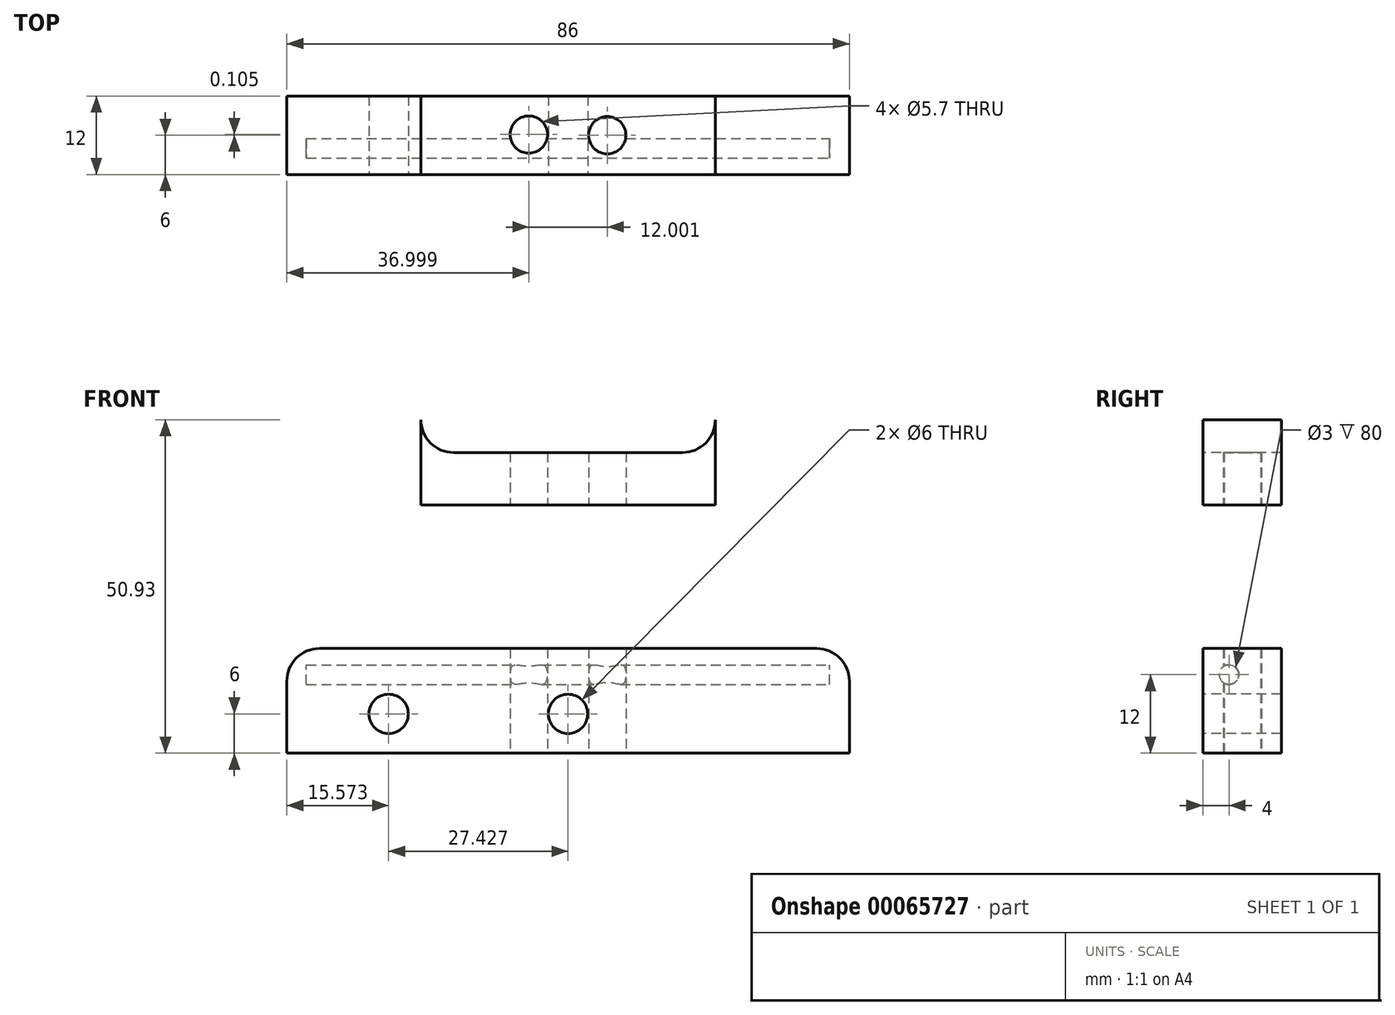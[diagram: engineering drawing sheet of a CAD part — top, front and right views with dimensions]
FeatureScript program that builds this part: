
annotation { "Feature Type Name" : "Feature", "Feature Type Description" : "" }
export const myFeature = defineFeature(function(context is Context, id is Id, definition is map)
    precondition{}
    {
        {
            var Q0;
            Q0=qCreatedBy(makeId("Top.planeOp"),FACE);
            var sketch = newSketch(context, id + "F0", { "sketchPlane" : qUnion([Q0])});
            skPoint(sketch, "E0.rect.middle", {"position": v(0, 0) * mm});
            skLineSegment(sketch, "E1", {"start": v(0, 0) * mm, "end": v(0, 2) * mm});
            skLineSegment(sketch, "E2", {"start": v(0, 2) * mm, "end": v(12, 2) * mm, "construction": true});
            skPoint(sketch, "E3.rect.middle", {"position": v(0, 2) * mm});
            skLineSegment(sketch, "E4", {"start": v(35, -4) * mm, "end": v(20.22, -4) * mm});
            skLineSegment(sketch, "E5", {"start": v(35, 8) * mm, "end": v(-35, 8) * mm});
            skPoint(sketch, "E6.rect.middle", {"position": v(0, 8) * mm});
            skLineSegment(sketch, "E7", {"start": v(-35, 8) * mm, "end": v(35, 8) * mm});
            skLineSegment(sketch, "E8.MirrorCS", {"start": v(19.85, 8) * mm, "end": v(20.22, 8) * mm});
            skLineSegment(sketch, "E9.trimOffspring", {"start": v(-20.22, -4) * mm, "end": v(-35, -4) * mm});
            skLineSegment(sketch, "E10.trimOffspring", {"start": v(19.85, -4) * mm, "end": v(-19.85, -4) * mm});
            skLineSegment(sketch, "E11", {"start": v(-19.85, -4) * mm, "end": v(-20.22, -4) * mm});
            skLineSegment(sketch, "E12", {"start": v(19.85, -4) * mm, "end": v(20.22, -4) * mm});
            skPoint(sketch, "E13.left.start.orphan", {"position": v(-19.85, 8) * mm});
            skPoint(sketch, "E14.start.orphan", {"position": v(-20.22, 8) * mm});
            skLineSegment(sketch, "E15.bottom", {"start": v(-35, 8) * mm, "end": v(-43, 8) * mm});
            skLineSegment(sketch, "E15.top", {"start": v(-35, -4) * mm, "end": v(-43, -4) * mm});
            skLineSegment(sketch, "E15.right", {"start": v(-43, 8) * mm, "end": v(-43, -4) * mm});
            skLineSegment(sketch, "E16.bottom", {"start": v(35, 8) * mm, "end": v(43, 8) * mm});
            skLineSegment(sketch, "E16.top", {"start": v(35, -4) * mm, "end": v(43, -4) * mm});
            skLineSegment(sketch, "E16.right", {"start": v(43, 8) * mm, "end": v(43, -4) * mm});
            skCircle(sketch, "E17", {"center": v(6, 2) * mm, "radius": 2.85 * mm});
            skCircle(sketch, "E18", {"center": v(-6, 2.1) * mm, "radius": 2.85 * mm});
            skSolve(sketch);
        }
        {
            var Q0;
            {var subQ4=sQuery(id+"F0.wireOp",EDGE,"E6.rect.right");Q0=makeQuery(id+"F0.imprint","IMPRINT",FACE,{"disambiguationData":[TD([[makeQuery(id+"F0.imprint","IMPRINT",EDGE,{"derivedFrom":subQ4}),1.0]])]});}
            var Q1;
            {var subQ3=sQuery(id+"F0.wireOp",EDGE,"E13.right");Q1=makeQuery(id+"F0.imprint","IMPRINT",FACE,{"disambiguationData":[TD([[makeQuery(id+"F0.imprint","IMPRINT",EDGE,{"derivedFrom":subQ3}),-1.0]])]});}
            var Q2;
            {var subQ5=sQuery(id+"F0.wireOp",EDGE,"E13.left");Q2=makeQuery(id+"F0.imprint","IMPRINT",FACE,{"disambiguationData":[TD([[makeQuery(id+"F0.imprint","IMPRINT",EDGE,{"derivedFrom":subQ5}),1.0]])]});}
            var Q3;
            Q3=makeQuery(id+"F0.imprint","IMPRINT",FACE,{"disambiguationData":[TD([[makeQuery(id+"F0.imprint","IMPRINT",EDGE,{"derivedFrom":sQuery(id+"F0.wireOp",EDGE,"58a1e8f5-9967-42e7-923e-22b4158e76640.MirrorC")}),1.0]])]});
            var Q4;
            Q4=makeQuery(id+"F0.imprint","IMPRINT",FACE,{"disambiguationData":[TD([[makeQuery(id+"F0.imprint","IMPRINT",EDGE,{"derivedFrom":sQuery(id+"F0.wireOp",EDGE,"58a1e8f5-9967-42e7-923e-22b4158e76640.MirrorC")}),-1.0]])]});
            var Q5;
            {var subQ0=sQuery(id+"F0.wireOp",EDGE,"E7");var subQ1=sQuery(id+"F0.wireOp",EDGE,"b3edcb3a-f617-4188-b1d9-e1a55aabad28");var subQ2=makeQuery(id+"F0.imprint","INTERSECT",VERTEX,{"derivedFrom":[subQ1,subQ0]});Q5=makeQuery(id+"F0.imprint","IMPRINT",FACE,{"disambiguationData":[TD([[makeQuery(id+"F0.imprint","IMPRINT",EDGE,{"disambiguationData":[TD([[subQ2,-1.0]])],"derivedFrom":subQ1}),-1.0]])]});}
            var Q6;
            Q6=makeQuery(id+"F0.imprint","IMPRINT",FACE,{"disambiguationData":[TD([[makeQuery(id+"F0.imprint","IMPRINT",EDGE,{"derivedFrom":sQuery(id+"F0.wireOp",EDGE,"0f5a9281-f327-4dc0-9b60-7cf9e87c13e7")}),-1.0]])]});
            var Q7;
            Q7=makeQuery(id+"F0.imprint","IMPRINT",FACE,{"disambiguationData":[TD([[makeQuery(id+"F0.imprint","IMPRINT",EDGE,{"derivedFrom":sQuery(id+"F0.wireOp",EDGE,"0f5a9281-f327-4dc0-9b60-7cf9e87c13e7")}),1.0]])]});
            var Q8;
            {var subQ0=sQuery(id+"F0.wireOp",EDGE,"7a62f623-bed4-47ff-af37-e2dce5c890c03.MirrorCS");Q8=makeQuery(id+"F0.imprint","IMPRINT",FACE,{"disambiguationData":[TD([[makeQuery(id+"F0.imprint","IMPRINT",EDGE,{"derivedFrom":subQ0}),-1.0]])]});}
            var Q9;
            {var subQ4=sQuery(id+"F0.wireOp",EDGE,"E4");Q9=makeQuery(id+"F0.imprint","IMPRINT",FACE,{"disambiguationData":[TD([[makeQuery(id+"F0.imprint","IMPRINT",EDGE,{"derivedFrom":subQ4}),-1.0]])]});}
            var Q10;
            {var subQ3=sQuery(id+"F0.wireOp",EDGE,"E6.rect.top");Q10=makeQuery(id+"F0.imprint","IMPRINT",FACE,{"disambiguationData":[TD([[makeQuery(id+"F0.imprint","IMPRINT",EDGE,{"derivedFrom":subQ3}),-1.0]])]});}
            var Q11;
            Q11=makeQuery(id+"F0.imprint","IMPRINT",FACE,{"disambiguationData":[TD([[makeQuery(id+"F0.imprint","IMPRINT",EDGE,{"derivedFrom":sQuery(id+"F0.wireOp",EDGE,"NbMli8i6-iFg7-sWmi-01Ci-sI5fGouLRfiF")}),-1.0]])]});
            var Q12;
            {var subQ0=sQuery(id+"F0.wireOp",EDGE,"E14");Q12=makeQuery(id+"F0.imprint","IMPRINT",FACE,{"disambiguationData":[TD([[makeQuery(id+"F0.imprint","IMPRINT",EDGE,{"derivedFrom":subQ0}),1.0]])]});}
            var Q13;
            {var subQ1=sQuery(id+"F0.wireOp",EDGE,"E3.rect.left");Q13=makeQuery(id+"F0.imprint","IMPRINT",FACE,{"disambiguationData":[TD([[makeQuery(id+"F0.imprint","IMPRINT",EDGE,{"derivedFrom":subQ1}),-1.0]])]});}
            var Q14;
            Q14=makeQuery(id+"F0.imprint","IMPRINT",FACE,{"disambiguationData":[TD([[makeQuery(id+"F0.imprint","IMPRINT",EDGE,{"derivedFrom":sQuery(id+"F0.wireOp",EDGE,"E9.trimOffspring")}),-1.0]])]});
            extrude(context, id + "F1", {"entities" : qUnion([Q0, Q1, Q2, Q3, Q4, Q5, Q6, Q7, Q8, Q9, Q10, Q11, Q12, Q13, Q14]), "depth" : 16 * mm});
        }
        {
            var Q0;
            Q0=qCreatedBy(makeId("Front.planeOp"),FACE);
            var sketch = newSketch(context, id + "F2", { "sketchPlane" : qUnion([Q0])});
            skLineSegment(sketch, "E19", {"start": v(0, 0) * mm, "end": v(0, 12) * mm});
            skLineSegment(sketch, "E20", {"start": v(0, 6) * mm, "end": v(-27.43, 6) * mm, "construction": true});
            skCircle(sketch, "E21", {"center": v(-27.43, 6) * mm, "radius": 3 * mm});
            skCircle(sketch, "E22.MirrorC", {"center": v(27.43, 6) * mm, "radius": 3 * mm});
            skLineSegment(sketch, "E23", {"start": v(0, 6) * mm, "end": v(52.55, 6) * mm, "construction": true});
            skLineSegment(sketch, "E24", {"start": v(0, 0) * mm, "end": v(-52.55, 0) * mm, "construction": true});
            skLineSegment(sketch, "E25", {"start": v(-52.55, 0) * mm, "end": v(-52.55, 5) * mm, "construction": true});
            skLineSegment(sketch, "E26", {"start": v(-52.55, 7.5) * mm, "end": v(-52.55, 5) * mm, "construction": true});
            skCircle(sketch, "E27", {"center": v(-52.55, 7.5) * mm, "radius": 2.5 * mm});
            skCircle(sketch, "E28.MirrorC", {"center": v(52.55, 7.5) * mm, "radius": 2.5 * mm});
            skCircle(sketch, "E29", {"center": v(0, 6) * mm, "radius": 3 * mm});
            skSolve(sketch);
        }
        {
            var Q0;
            Q0=makeQuery(id+"F2.imprint","IMPRINT",FACE,{"disambiguationData":[TD([[makeQuery(id+"F2.imprint","IMPRINT",EDGE,{"derivedFrom":sQuery(id+"F2.wireOp",EDGE,"E21")}),1.0]])]});
            var Q1;
            Q1=makeQuery(id+"F2.imprint","IMPRINT",FACE,{"disambiguationData":[TD([[makeQuery(id+"F2.imprint","IMPRINT",EDGE,{"derivedFrom":sQuery(id+"F2.wireOp",EDGE,"E22.MirrorC")}),-1.0]])]});
            var Q2;
            {var subQ0=sQuery(id+"F2.wireOp",EDGE,"E29");var subQ1=sQuery(id+"F2.wireOp",EDGE,"E19");var subQ2=makeQuery(id+"F2.imprint","INTERSECT",VERTEX,{"disambiguationData":[OD(0.0)],"derivedFrom":[subQ1,subQ0]});Q2=makeQuery(id+"F2.imprint","IMPRINT",FACE,{"disambiguationData":[TD([[makeQuery(id+"F2.imprint","IMPRINT",EDGE,{"disambiguationData":[TD([[subQ2,-1.0]])],"derivedFrom":subQ1}),1.0]])]});}
            var Q3;
            {var subQ0=sQuery(id+"F2.wireOp",EDGE,"E29");var subQ1=sQuery(id+"F2.wireOp",EDGE,"E19");var subQ2=makeQuery(id+"F2.imprint","INTERSECT",VERTEX,{"disambiguationData":[OD(0.0)],"derivedFrom":[subQ1,subQ0]});Q3=makeQuery(id+"F2.imprint","IMPRINT",FACE,{"disambiguationData":[TD([[makeQuery(id+"F2.imprint","IMPRINT",EDGE,{"disambiguationData":[TD([[subQ2,-1.0]])],"derivedFrom":subQ1}),-1.0]])]});}
            extrude(context, id + "F3", {"entities" : qUnion([Q0, Q1, Q2, Q3]), "operationType" : NewBodyOperationType.REMOVE, "oppositeDirection" : true, "depth" : 25 * mm, "symmetric" : true});
        }
        {
            var Q0;
            Q0=qCreatedBy(makeId("Right.planeOp"),FACE);
            var sketch = newSketch(context, id + "F4", { "sketchPlane" : qUnion([Q0])});
            skLineSegment(sketch, "E30", {"start": v(0, 0) * mm, "end": v(0, 12) * mm});
            skCircle(sketch, "E31", {"center": v(0, 12) * mm, "radius": 1.5 * mm});
            skSolve(sketch);
        }
        {
            var Q0;
            Q0=qSketchRegion(id+"F4",true);
            extrude(context, id + "F5", {"entities" : qUnion([Q0]), "operationType" : NewBodyOperationType.REMOVE, "oppositeDirection" : true, "depth" : 80 * mm, "symmetric" : true});
        }
        {
            var Q0;
            Q0=qCreatedBy(makeId("Front.planeOp"),FACE);
            var sketch = newSketch(context, id + "F6", { "sketchPlane" : qUnion([Q0])});
            skLineSegment(sketch, "E32.bottom", {"start": v(-22.5, 37.93) * mm, "end": v(22.5, 37.93) * mm});
            skLineSegment(sketch, "E32.top", {"start": v(-17.5, 45.93) * mm, "end": v(17.5, 45.93) * mm});
            skLineSegment(sketch, "E32.right", {"start": v(22.5, 37.93) * mm, "end": v(22.5, 45.93) * mm});
            skPoint(sketch, "E32.middle", {"position": v(0, 41.93) * mm});
            skPoint(sketch, "E33.visualSharp", {"position": v(-22.5, 45.93) * mm});
            skArc(sketch, "E33.filletArc", {"start": v(-22.5, 50.93) * mm, "mid": v(-21.04, 47.4) * mm, "end": v(-17.5, 45.93) * mm});
            skLineSegment(sketch, "E34", {"start": v(-22.5, 50.93) * mm, "end": v(-22.5, 37.93) * mm});
            skLineSegment(sketch, "E35", {"start": v(0, 45.93) * mm, "end": v(0, 48.76) * mm, "construction": true});
            skArc(sketch, "E36.MirrorCS", {"start": v(22.5, 50.93) * mm, "mid": v(21.04, 47.4) * mm, "end": v(17.5, 45.93) * mm});
            skLineSegment(sketch, "E37", {"start": v(22.5, 50.93) * mm, "end": v(22.5, 45.93) * mm});
            skSolve(sketch);
        }
        {
            var Q0;
            Q0 = qSketchRegion(id + "F6", true);
            var Q1;
            Q1=makeQuery(id+"F1.opExtrude","SWEPT_FACE",FACE,{"disambiguationData":[OSD([sQuery(id+"F0.wireOp",EDGE,"E7"),sQuery(id+"F0.wireOp",EDGE,"E8.MirrorCS"),sQuery(id+"F0.wireOp",EDGE,"E15.bottom"),sQuery(id+"F0.wireOp",EDGE,"E16.bottom")])]});
            var Q2;
            Q2=makeQuery(id+"F1.opExtrude","SWEPT_FACE",FACE,{"disambiguationData":[OSD([sQuery(id+"F0.wireOp",EDGE,"E4"),sQuery(id+"F0.wireOp",EDGE,"E9.trimOffspring"),sQuery(id+"F0.wireOp",EDGE,"E10.trimOffspring"),sQuery(id+"F0.wireOp",EDGE,"E11"),sQuery(id+"F0.wireOp",EDGE,"E12"),sQuery(id+"F0.wireOp",EDGE,"E15.top"),sQuery(id+"F0.wireOp",EDGE,"E16.top")])]});
            extrude(context, id + "F7", {"entities" : qUnion([Q0]), "endBound" : BoundingType.UP_TO_SURFACE, "oppositeDirection" : true, "endBoundEntityFace" : qUnion([Q1]), "depth" : 8 * mm, "hasSecondDirection" : true, "secondDirectionBound" : BoundingType.UP_TO_SURFACE, "secondDirectionOppositeDirection" : false, "secondDirectionBoundEntityFace" : qUnion([Q2]), "secondDirectionDepth" : 25 * mm});
        }
        {
            var Q0;
            Q0=makeQuery(id+"F0.imprint","IMPRINT",FACE,{"disambiguationData":[TD([[makeQuery(id+"F0.imprint","IMPRINT",EDGE,{"derivedFrom":sQuery(id+"F0.wireOp",EDGE,"E18")}),1.0]])]});
            var Q1;
            Q1=makeQuery(id+"F0.imprint","IMPRINT",FACE,{"disambiguationData":[TD([[makeQuery(id+"F0.imprint","IMPRINT",EDGE,{"derivedFrom":sQuery(id+"F0.wireOp",EDGE,"E17")}),1.0]])]});
            extrude(context, id + "F8", {"entities" : qUnion([Q0, Q1]), "operationType" : NewBodyOperationType.REMOVE, "endBound" : BoundingType.THROUGH_ALL, "depth" : 25 * mm});
        }
        {
            var Q0;
            Q0=makeQuery(id+"F1.opExtrude","CAP_EDGE",EDGE,{"disambiguationData":[OSD([sQuery(id+"F0.wireOp",EDGE,"E15.right")])],"isStart":false});
            var Q1;
            Q1=makeQuery(id+"F1.opExtrude","CAP_EDGE",EDGE,{"disambiguationData":[OSD([sQuery(id+"F0.wireOp",EDGE,"E16.right")])],"isStart":false});
            fillet(context, id + "F9", {"entities" : qUnion([Q0, Q1]), "radius" : 5 * mm, "tangentPropagation" : true, "allowEdgeOverflow" : false});
        }
    });
